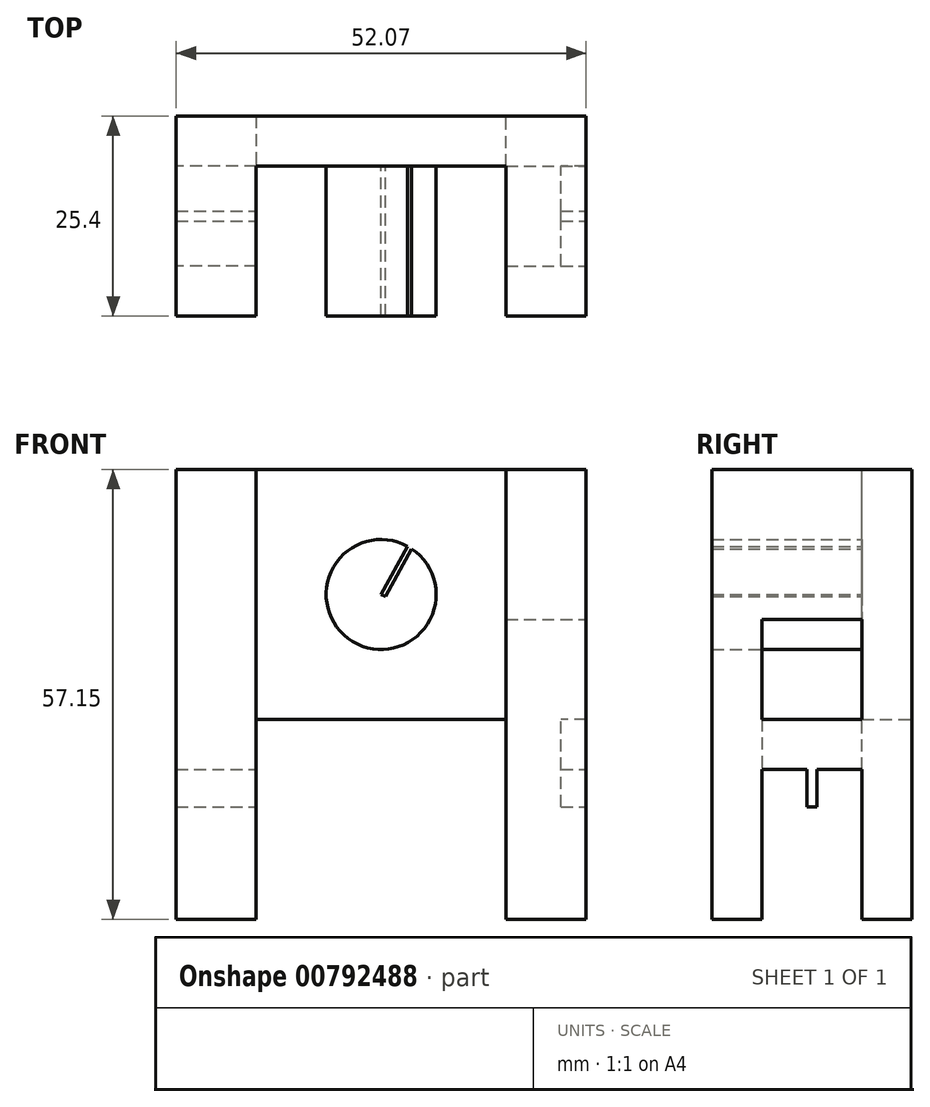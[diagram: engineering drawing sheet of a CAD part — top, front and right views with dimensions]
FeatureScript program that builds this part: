
annotation { "Feature Type Name" : "Feature", "Feature Type Description" : "" }
export const myFeature = defineFeature(function(context is Context, id is Id, definition is map)
    precondition{}
    {
        {
            var Q0;
            Q0=qCreatedBy(makeId("Front.planeOp"),FACE);
            var sketch = newSketch(context, id + "F0", { "sketchPlane" : qUnion([Q0])});
            skLineSegment(sketch, "E0.bottom", {"start": v(0, 0) * mm, "end": v(31.75, 0) * mm});
            skLineSegment(sketch, "E0.top", {"start": v(0, 31.75) * mm, "end": v(31.75, 31.75) * mm});
            skLineSegment(sketch, "E0.left", {"start": v(0, 0) * mm, "end": v(0, 31.75) * mm});
            skLineSegment(sketch, "E0.right", {"start": v(31.75, 0) * mm, "end": v(31.75, 31.75) * mm});
            skSolve(sketch);
        }
        {
            var Q0;
            Q0=makeQuery(id+"F0.imprint","IMPRINT",FACE,{"disambiguationData":[TD([[makeQuery(id+"F0.imprint","IMPRINT",EDGE,{"derivedFrom":sQuery(id+"F0.wireOp",EDGE,"E0.bottom")}),1.0]])]});
            extrude(context, id + "F1", {"entities" : qUnion([Q0]), "depth" : 6.35 * mm, "offsetDistance" : 25.4 * mm});
        }
        {
            var Q0;
            Q0=makeQuery(id+"F1.opExtrude","SWEPT_FACE",FACE,{"disambiguationData":[OSD([sQuery(id+"F0.wireOp",EDGE,"E0.left")])]});
            var sketch = newSketch(context, id + "F2", { "sketchPlane" : qUnion([Q0])});
            skLineSegment(sketch, "E1.bottom", {"start": v(0, -25.4) * mm, "end": v(25.4, -25.4) * mm});
            skLineSegment(sketch, "E1.top", {"start": v(0, 31.75) * mm, "end": v(25.4, 31.75) * mm});
            skLineSegment(sketch, "E1.left", {"start": v(0, -25.4) * mm, "end": v(0, 31.75) * mm});
            skLineSegment(sketch, "E1.right", {"start": v(25.4, -25.4) * mm, "end": v(25.4, 31.75) * mm});
            skSolve(sketch);
        }
        {
            var Q0;
            {var subQ3=sQuery(id+"F2.wireOp",EDGE,"E1.bottom");Q0=makeQuery(id+"F2.imprint","IMPRINT",FACE,{"disambiguationData":[TD([[makeQuery(id+"F2.imprint","IMPRINT",EDGE,{"derivedFrom":subQ3}),1.0]])]});}
            var Q1;
            {var subQ3=sQuery(id+"F0.wireOp",EDGE,"E0.left");var subQ4=makeQuery(id+"F1.opExtrude","CAP_EDGE",EDGE,{"disambiguationData":[OSD([subQ3])],"isStart":false});Q1=makeQuery(id+"F2.imprint","IMPRINT",FACE,{"disambiguationData":[TD([[makeQuery(id+"F2.imprint","IMPRINT",EDGE,{"derivedFrom":subQ4}),1.0]])]});}
            extrude(context, id + "F3", {"entities" : qUnion([Q0, Q1]), "operationType" : NewBodyOperationType.ADD, "depth" : 10.16 * mm, "offsetDistance" : 25.4 * mm});
        }
        {
            var Q0;
            Q0=makeQuery(id+"F1.opExtrude","SWEPT_FACE",FACE,{"disambiguationData":[OSD([sQuery(id+"F0.wireOp",EDGE,"E0.right")])]});
            var sketch = newSketch(context, id + "F4", { "sketchPlane" : qUnion([Q0])});
            skLineSegment(sketch, "E2.bottom", {"start": v(0, 31.75) * mm, "end": v(-25.4, 31.75) * mm});
            skLineSegment(sketch, "E2.top", {"start": v(0, -25.4) * mm, "end": v(-25.4, -25.4) * mm});
            skLineSegment(sketch, "E2.left", {"start": v(0, 31.75) * mm, "end": v(0, -25.4) * mm});
            skLineSegment(sketch, "E2.right", {"start": v(-25.4, 31.75) * mm, "end": v(-25.4, -25.4) * mm});
            skSolve(sketch);
        }
        {
            var Q0;
            {var subQ3=sQuery(id+"F0.wireOp",EDGE,"E0.right");var subQ4=makeQuery(id+"F1.opExtrude","CAP_EDGE",EDGE,{"disambiguationData":[OSD([subQ3])],"isStart":false});Q0=makeQuery(id+"F4.imprint","IMPRINT",FACE,{"disambiguationData":[TD([[makeQuery(id+"F4.imprint","IMPRINT",EDGE,{"derivedFrom":subQ4}),-1.0]])]});}
            var Q1;
            {var subQ3=sQuery(id+"F4.wireOp",EDGE,"E2.top");Q1=makeQuery(id+"F4.imprint","IMPRINT",FACE,{"disambiguationData":[TD([[makeQuery(id+"F4.imprint","IMPRINT",EDGE,{"derivedFrom":subQ3}),-1.0]])]});}
            extrude(context, id + "F5", {"entities" : qUnion([Q0, Q1]), "operationType" : NewBodyOperationType.ADD, "depth" : 10.16 * mm, "offsetDistance" : 25.4 * mm});
        }
        {
            var Q0;
            Q0=makeQuery(id+"F5.opExtrude","CAP_FACE",FACE,{"disambiguationData":[OSD([sQuery(id+"F4.wireOp",EDGE,"E2.bottom"),sQuery(id+"F4.wireOp",EDGE,"E2.top"),sQuery(id+"F4.wireOp",EDGE,"E2.left"),sQuery(id+"F4.wireOp",EDGE,"E2.right")])],"isStart":false});
            var sketch = newSketch(context, id + "F6", { "sketchPlane" : qUnion([Q0])});
            skLineSegment(sketch, "E3.bottom", {"start": v(-19.05, -25.4) * mm, "end": v(-6.35, -25.4) * mm});
            skLineSegment(sketch, "E3.top", {"start": v(-19.05, 12.7) * mm, "end": v(-6.35, 12.7) * mm});
            skLineSegment(sketch, "E3.left", {"start": v(-19.05, -25.4) * mm, "end": v(-19.05, 12.7) * mm});
            skLineSegment(sketch, "E3.right", {"start": v(-6.35, -25.4) * mm, "end": v(-6.35, 12.7) * mm});
            skSolve(sketch);
        }
        {
            var Q0;
            Q0=qSketchRegion(id+"F6",true);
            extrude(context, id + "F7", {"entities" : qUnion([Q0]), "operationType" : NewBodyOperationType.REMOVE, "oppositeDirection" : true, "depth" : 12.7 * mm, "offsetDistance" : 25.4 * mm});
        }
        {
            var Q0;
            Q0=makeQuery(id+"F7.boolean.opBoolean","MERGE",FACE,{"derivedFrom":[makeQuery(id+"F1.opExtrude","CAP_FACE",FACE,{"disambiguationData":[OSD([sQuery(id+"F0.wireOp",EDGE,"E0.bottom"),sQuery(id+"F0.wireOp",EDGE,"E0.top"),sQuery(id+"F0.wireOp",EDGE,"E0.left"),sQuery(id+"F0.wireOp",EDGE,"E0.right")])],"isStart":false}),makeQuery(id+"F7.opExtrude","SWEPT_FACE",FACE,{"disambiguationData":[OSD([sQuery(id+"F6.wireOp",EDGE,"E3.right")])]})]});
            var sketch = newSketch(context, id + "F8", { "sketchPlane" : qUnion([Q0])});
            skLineSegment(sketch, "E4.bottom", {"start": v(41.91, -6.35) * mm, "end": v(38.74, -6.35) * mm});
            skLineSegment(sketch, "E4.top", {"start": v(41.91, 0) * mm, "end": v(38.74, 0) * mm});
            skLineSegment(sketch, "E4.left", {"start": v(41.91, -6.35) * mm, "end": v(41.91, 0) * mm});
            skLineSegment(sketch, "E4.right", {"start": v(38.74, -6.35) * mm, "end": v(38.74, 0) * mm});
            skSolve(sketch);
        }
        {
            var Q0;
            Q0=makeQuery(id+"F8.imprint","IMPRINT",FACE,{"disambiguationData":[TD([[makeQuery(id+"F8.imprint","IMPRINT",EDGE,{"derivedFrom":sQuery(id+"F8.wireOp",EDGE,"E4.bottom")}),-1.0]])]});
            extrude(context, id + "F9", {"entities" : qUnion([Q0]), "operationType" : NewBodyOperationType.ADD, "endBound" : BoundingType.UP_TO_NEXT, "depth" : 25.4 * mm, "offsetDistance" : 25.4 * mm});
        }
        {
            var Q0;
            Q0=makeQuery(id+"F3.opExtrude","CAP_FACE",FACE,{"disambiguationData":[OSD([sQuery(id+"F2.wireOp",EDGE,"E1.bottom"),sQuery(id+"F2.wireOp",EDGE,"E1.top"),sQuery(id+"F2.wireOp",EDGE,"E1.left"),sQuery(id+"F2.wireOp",EDGE,"E1.right")])],"isStart":false});
            var sketch = newSketch(context, id + "F10", { "sketchPlane" : qUnion([Q0])});
            skLineSegment(sketch, "E5.bottom", {"start": v(6.35, -25.4) * mm, "end": v(19.05, -25.4) * mm});
            skLineSegment(sketch, "E5.top", {"start": v(6.35, -6.35) * mm, "end": v(19.05, -6.35) * mm});
            skLineSegment(sketch, "E5.left", {"start": v(6.35, -25.4) * mm, "end": v(6.35, -6.35) * mm});
            skLineSegment(sketch, "E5.right", {"start": v(19.05, -25.4) * mm, "end": v(19.05, -6.35) * mm});
            skSolve(sketch);
        }
        {
            var Q0;
            Q0=qSketchRegion(id+"F10",true);
            extrude(context, id + "F11", {"entities" : qUnion([Q0]), "operationType" : NewBodyOperationType.REMOVE, "oppositeDirection" : true, "depth" : 12.7 * mm, "offsetDistance" : 25.4 * mm});
        }
        {
            var Q0;
            Q0=makeQuery(id+"F7.boolean.opBoolean","MERGE",FACE,{"derivedFrom":[makeQuery(id+"F1.opExtrude","CAP_FACE",FACE,{"disambiguationData":[OSD([sQuery(id+"F0.wireOp",EDGE,"E0.bottom"),sQuery(id+"F0.wireOp",EDGE,"E0.top"),sQuery(id+"F0.wireOp",EDGE,"E0.left"),sQuery(id+"F0.wireOp",EDGE,"E0.right")])],"isStart":false}),makeQuery(id+"F7.opExtrude","SWEPT_FACE",FACE,{"disambiguationData":[OSD([sQuery(id+"F6.wireOp",EDGE,"E3.right")])]})]});
            var sketch = newSketch(context, id + "F12", { "sketchPlane" : qUnion([Q0])});
            skLineSegment(sketch, "E6", {"start": v(31.75, 12.7) * mm, "end": v(31.75, 0) * mm, "construction": true});
            skSolve(sketch);
        }
        {
            var Q0;
            Q0=makeQuery(id+"F11.boolean.opBoolean","COPY",FACE,{"derivedFrom":makeQuery(id+"F11.opExtrude","SWEPT_FACE",FACE,{"disambiguationData":[OSD([sQuery(id+"F10.wireOp",EDGE,"E5.top")])]})});
            var sketch = newSketch(context, id + "F13", { "sketchPlane" : qUnion([Q0])});
            skLineSegment(sketch, "E7.bottom", {"start": v(-10.16, 12.06) * mm, "end": v(0, 12.06) * mm});
            skLineSegment(sketch, "E7.top", {"start": v(-10.16, 13.33) * mm, "end": v(0, 13.33) * mm});
            skLineSegment(sketch, "E7.left", {"start": v(-10.16, 12.06) * mm, "end": v(-10.16, 13.33) * mm});
            skLineSegment(sketch, "E7.right", {"start": v(0, 12.06) * mm, "end": v(0, 13.33) * mm});
            skLineSegment(sketch, "E8", {"start": v(-10.16, 12.7) * mm, "end": v(0, 12.7) * mm, "construction": true});
            skSolve(sketch);
        }
        {
            var Q0;
            Q0=qSketchRegion(id+"F13",true);
            extrude(context, id + "F14", {"entities" : qUnion([Q0]), "operationType" : NewBodyOperationType.ADD, "depth" : 4.76 * mm, "offsetDistance" : 25.4 * mm});
        }
        {
            var Q0;
            {var subQ10=sQuery(id+"F0.wireOp",EDGE,"E0.top");Q0=makeQuery(id+"F12.imprint","IMPRINT",FACE,{"disambiguationData":[TD([[makeQuery(id+"F12.imprint","IMPRINT",EDGE,{"derivedFrom":makeQuery(id+"F1.opExtrude","CAP_EDGE",EDGE,{"disambiguationData":[OSD([subQ10])],"isStart":false})}),-1.0]])]});}
            var sketch = newSketch(context, id + "F15", { "sketchPlane" : qUnion([Q0])});
            skLineSegment(sketch, "E9", {"start": v(15.88, 15.87) * mm, "end": v(19.25, 22) * mm});
            skLineSegment(sketch, "E10", {"start": v(19.75, 21.68) * mm, "end": v(16.42, 15.63) * mm});
            skLineSegment(sketch, "E11", {"start": v(15.88, 15.87) * mm, "end": v(16.42, 15.63) * mm});
            skArc(sketch, "E12", {"start": v(19.25, 22) * mm, "mid": v(12.25, 9.9) * mm, "end": v(19.75, 21.68) * mm});
            skArc(sketch, "E13", {"start": v(19.75, 21.68) * mm, "mid": v(19.5, 21.84) * mm, "end": v(19.25, 22) * mm});
            skSolve(sketch);
        }
        {
            var Q0;
            Q0=makeQuery(id+"F15.imprint","IMPRINT",FACE,{"disambiguationData":[TD([[makeQuery(id+"F15.imprint","IMPRINT",EDGE,{"derivedFrom":sQuery(id+"F15.wireOp",EDGE,"E9")}),1.0]])]});
            extrude(context, id + "F16", {"entities" : qUnion([Q0]), "operationType" : NewBodyOperationType.ADD, "depth" : 19.05 * mm, "offsetDistance" : 25.4 * mm});
        }
        {
            var Q0;
            Q0=makeQuery(id+"F9.opExtrude","SWEPT_FACE",FACE,{"disambiguationData":[OSD([sQuery(id+"F8.wireOp",EDGE,"E4.bottom")])]});
            var sketch = newSketch(context, id + "F17", { "sketchPlane" : qUnion([Q0])});
            skLineSegment(sketch, "E14.bottom", {"start": v(38.74, 12.07) * mm, "end": v(41.91, 12.07) * mm});
            skLineSegment(sketch, "E14.top", {"start": v(38.74, 13.34) * mm, "end": v(41.91, 13.34) * mm});
            skLineSegment(sketch, "E14.left", {"start": v(38.74, 12.07) * mm, "end": v(38.74, 13.34) * mm});
            skLineSegment(sketch, "E14.right", {"start": v(41.91, 12.07) * mm, "end": v(41.91, 13.34) * mm});
            skLineSegment(sketch, "E15", {"start": v(38.74, 12.7) * mm, "end": v(41.91, 12.7) * mm, "construction": true});
            skSolve(sketch);
        }
        {
            var Q0;
            Q0=qSketchRegion(id+"F17",true);
            extrude(context, id + "F18", {"entities" : qUnion([Q0]), "operationType" : NewBodyOperationType.ADD, "depth" : 4.75 * mm, "offsetDistance" : 25.4 * mm});
        }
    });
